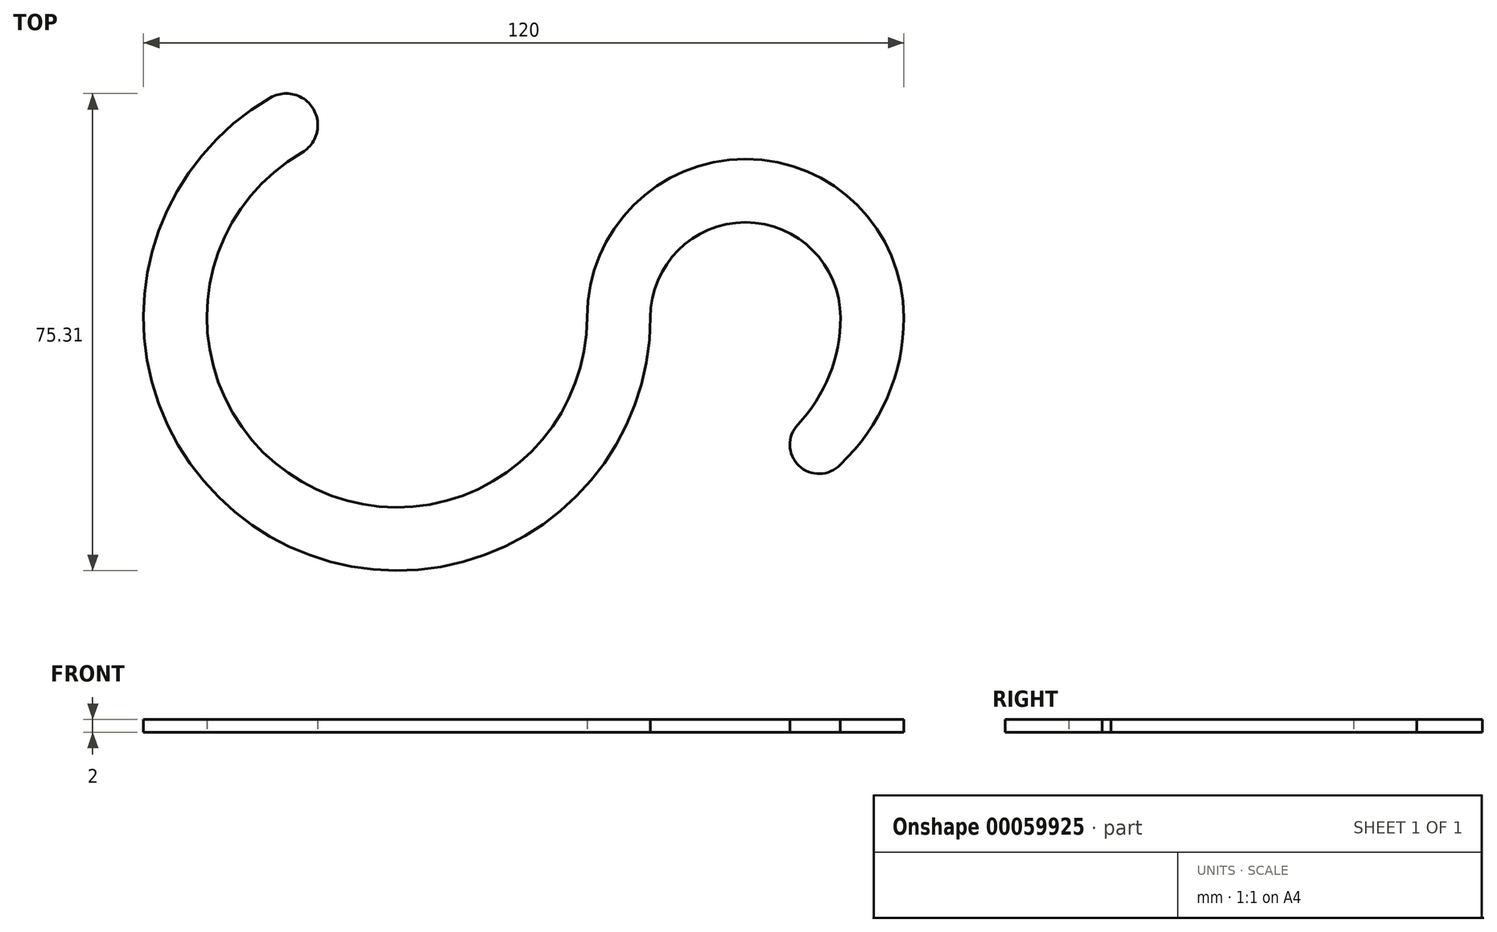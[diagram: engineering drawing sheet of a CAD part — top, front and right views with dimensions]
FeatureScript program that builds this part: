
annotation { "Feature Type Name" : "Feature", "Feature Type Description" : "" }
export const myFeature = defineFeature(function(context is Context, id is Id, definition is map)
    precondition{}
    {
        {
            var Q0;
            Q0=qCreatedBy(makeId("Top.planeOp"),FACE);
            var sketch = newSketch(context, id + "F0", { "sketchPlane" : qUnion([Q0])});
            skPoint(sketch, "E0", {"position": v(0, 0) * mm});
            skArc(sketch, "E1", {"start": v(15, 0) * mm, "mid": v(0, 15) * mm, "end": v(-15, 0) * mm});
            skArc(sketch, "E2", {"start": v(-85, 0) * mm, "mid": v(-55, -29.97) * mm, "end": v(-25, 0) * mm});
            skArc(sketch, "E3", {"start": v(-95, 0) * mm, "mid": v(-55, -39.97) * mm, "end": v(-15, 0) * mm});
            skArc(sketch, "E4", {"start": v(-85, 0) * mm, "mid": v(-80.99, 15.02) * mm, "end": v(-70, 26) * mm});
            skArc(sketch, "E5", {"start": v(-95, 0) * mm, "mid": v(-89.65, 20.02) * mm, "end": v(-75, 34.67) * mm});
            skArc(sketch, "E6", {"start": v(-70, 26) * mm, "mid": v(-68.17, 32.84) * mm, "end": v(-75, 34.67) * mm});
            skPoint(sketch, "E7", {"position": v(-20, 0) * mm});
            skArc(sketch, "E8", {"start": v(-25, 0) * mm, "mid": v(0, 25) * mm, "end": v(25, 0) * mm});
            skLineSegment(sketch, "E9", {"start": v(-26.02, -7.74) * mm, "end": v(-16.36, -10.32) * mm});
            skArc(sketch, "E10", {"start": v(8.27, -16.92) * mm, "mid": v(13.26, -9.1) * mm, "end": v(15, 0) * mm});
            skArc(sketch, "E11", {"start": v(18.27, -19.6) * mm, "mid": v(23.27, -10.36) * mm, "end": v(25, 0) * mm});
            skLineSegment(sketch, "E12", {"start": v(8.27, -16.92) * mm, "end": v(14.95, -23.24) * mm});
            skArc(sketch, "E13", {"start": v(18.27, -19.6) * mm, "mid": v(16.68, -21.49) * mm, "end": v(14.95, -23.24) * mm});
            skArc(sketch, "E14", {"start": v(8.27, -16.92) * mm, "mid": v(8.45, -23.43) * mm, "end": v(14.95, -23.24) * mm});
            skLineSegment(sketch, "E15.trimOffspring", {"start": v(8.27, -16.92) * mm, "end": v(18.27, -19.6) * mm});
            skPoint(sketch, "E16.start.orphan", {"position": v(10.5, 0) * mm});
            skSolve(sketch);
        }
        {
            var Q0;
            Q0 = qSketchRegion(id + "F0", true);
            extrude(context, id + "F1", {"entities" : qUnion([Q0]), "depth" : 2 * mm});
        }
    });
